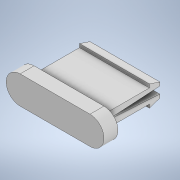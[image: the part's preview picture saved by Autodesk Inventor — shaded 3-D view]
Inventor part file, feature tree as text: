
AUTODESK INVENTOR PART (.ipt)
format: ipt  version: 2020.3 (Build 243373000, 373)  size: 133,632 bytes
history: native  units: mm
features: extrude x4, sketch x4
ambient origin geometry x8: Origin, YZ Plane, XZ Plane, XY Plane, X Axis, Y Axis, Z Axis, Center Point
bodies: Solid1 (feature_tree)
feature tree (8):
  extrude  "Extrusion1"  Depth=8.0mm TaperAngle=0.0deg
  extrude  "Extrusion2"  Depth=1.5mm
  extrude  "Extrusion3"  Depth=10.0mm TaperAngle=0.0deg
  extrude  "Extrusion4"  Depth=2.0mm
  sketch  "Sketch1"  dims[d3=2.0mm d4=0.0mm d6=8.0mm d7=0.0mm]
  sketch  "Sketch2"  dims[d8=1.5mm d9=0.5mm]
  sketch  "Sketch3"  dims[d10=0.5mm d11=10.0mm d12=0.0mm]
  sketch  "Sketch4"  dims[d13=0.5mm d14=0.5mm d15=2.0mm d16=0.0mm]
